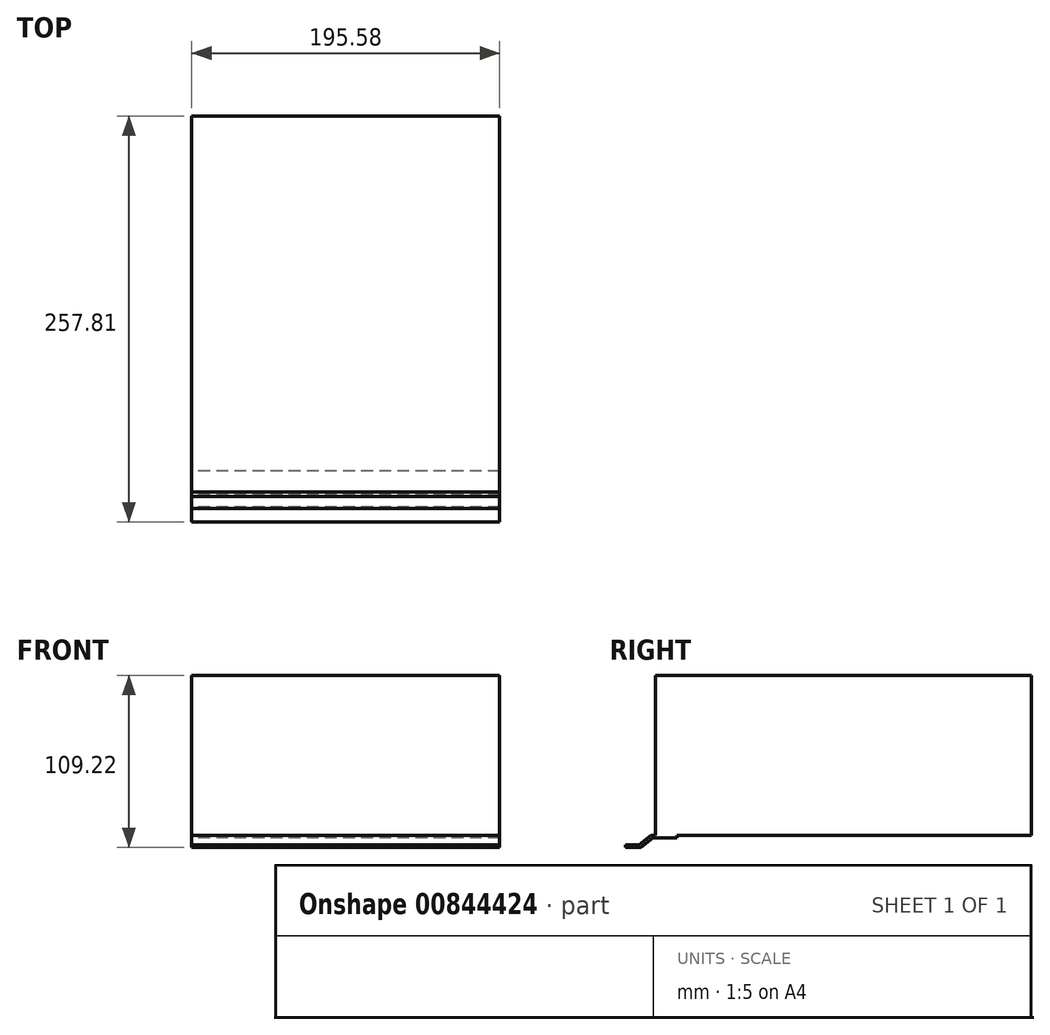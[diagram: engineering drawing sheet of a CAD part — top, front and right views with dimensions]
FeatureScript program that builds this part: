
annotation { "Feature Type Name" : "Feature", "Feature Type Description" : "" }
export const myFeature = defineFeature(function(context is Context, id is Id, definition is map)
    precondition{}
    {
        {
            var Q0;
            Q0=qCreatedBy(makeId("Top.planeOp"),FACE);
            var sketch = newSketch(context, id + "F0", { "sketchPlane" : qUnion([Q0])});
            skLineSegment(sketch, "E0.bottom", {"start": v(97.8, 119.38) * mm, "end": v(-97.8, 119.38) * mm});
            skLineSegment(sketch, "E0.top", {"start": v(97.8, -119.38) * mm, "end": v(-97.8, -119.38) * mm});
            skLineSegment(sketch, "E0.left", {"start": v(97.8, 119.38) * mm, "end": v(97.8, -119.38) * mm});
            skLineSegment(sketch, "E0.right", {"start": v(-97.8, 119.38) * mm, "end": v(-97.8, -119.38) * mm});
            skPoint(sketch, "E0.middle", {"position": v(0, 0) * mm});
            skSolve(sketch);
        }
        {
            var Q0;
            Q0 = qSketchRegion(id + "F0", true);
            extrude(context, id + "F1", {"entities" : qUnion([Q0]), "depth" : 101.6 * mm, "offsetDistance" : 25.4 * mm});
        }
        {
            var Q0;
            Q0=makeQuery(id+"F1.opExtrude","SWEPT_FACE",FACE,{"disambiguationData":[OSD([sQuery(id+"F0.wireOp",EDGE,"E0.right")])]});
            var sketch = newSketch(context, id + "F2", { "sketchPlane" : qUnion([Q0])});
            skLineSegment(sketch, "E1", {"start": v(105.9, 0) * mm, "end": v(122.35, 0) * mm});
            skLineSegment(sketch, "E2", {"start": v(122.35, 0) * mm, "end": v(129.94, -6.03) * mm});
            skLineSegment(sketch, "E3", {"start": v(129.94, -6.03) * mm, "end": v(138.43, -6.03) * mm});
            skLineSegment(sketch, "E4", {"start": v(138.43, -6.03) * mm, "end": v(138.43, -7.62) * mm});
            skLineSegment(sketch, "E5", {"start": v(138.43, -7.62) * mm, "end": v(128.8, -7.62) * mm});
            skLineSegment(sketch, "E6", {"start": v(128.8, -7.62) * mm, "end": v(121.2, -1.59) * mm});
            skLineSegment(sketch, "E7", {"start": v(121.2, -1.59) * mm, "end": v(105.9, -1.59) * mm});
            skLineSegment(sketch, "E8", {"start": v(105.9, -1.59) * mm, "end": v(105.9, 0) * mm});
            skSolve(sketch);
        }
        {
            var Q0;
            Q0 = qSketchRegion(id + "F2", true);
            extrude(context, id + "F3", {"entities" : qUnion([Q0]), "operationType" : NewBodyOperationType.ADD, "oppositeDirection" : true, "depth" : 195.58 * mm, "offsetDistance" : 25.4 * mm});
        }
    });
